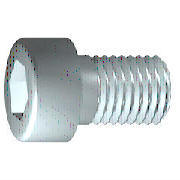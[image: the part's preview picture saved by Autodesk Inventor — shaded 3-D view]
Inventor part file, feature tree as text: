
AUTODESK INVENTOR PART (.ipt)
format: ipt  version: 2013 (Build 170138000, 138)  size: 189,952 bytes
history: native  units: mm (DEFAULTED — no unit token found)
features: sketch x2, extrude x1, plane x1, fillet x1
ambient origin geometry x7: Origin, YZ Plane, XY Plane, X Axis, Y Axis, Z Axis, Center Point
bodies: Solid1 (feature_tree), Body (feature_tree)
feature tree (5):
  extrude  "Slot"  Depth=0.306825mm
  plane  "Work Plane1"
  fillet  "Fillet2"  Radius=3.0mm
  sketch  "Sketch1"  dims[d1=8.75mm d2=0.306825mm d3=3.0mm]
  sketch  "Sketch2"  dims[d4=1.3mm d5=60.0deg d6=3.0mm d7=3.0mm d8=2.886751mm d9=5.5mm d10=90.0deg d11=10.0mm d12=0.0mm d13=8.75mm d14=0.0mm d15=0.306725mm d16=0.306725mm d17=0.3mm d19=0.0mm d26=10.0mm d27=45.0deg d28=0.0mm d29=0.0mm d30=0.1mm]
